# Revit family: LIANO II COMPACT TWIN SHWR 3S OHD
name_source: partatom
category: Plumbing Fixtures
units: mm (PartAtom-declared; Revit-internal decimal feet)

## family parameters
Cut with Voids When Loaded = No
Host = Face
OmniClass Number = 23.45.05.14.17
OmniClass Title = Showers
Part Type = Normal
Room Calculation Point = No
Round Connector Dimension = Use Diameter
Shared = No

## types (6) — shared parameters
Assembly Code = D2020300
CW Connection = Yes
HW Connection = Yes
Manufacturer = GWA Bathrooms & Kitchens
Material_Sprays = GWA-Plastic-General
URL = https://www.caroma.com.au
Vent Connection = No
Waste Connection = No
zero-valued in all types: Default Elevation

## per-type parameters (varying)
| type | Material_Base | Model |
| LIANO II COMPACT TWIN SHWR 3S OHD CH | GWA_Metal-Chrome | 96472C33A |
| LIANO II COMPACT TWIN SHWR 3S OHD BB | GWA_Metal-Brushed-Brass | 96472BB33A |
| LIANO II COMPACT TWIN SHWR 3S OHD BK | GWA-Metal-Black | 96472B33A |
| LIANO II COMPACT TWIN SHWR 3S OHD GM | GWA_Metal-Brushed-Gunmetal | 96472GM33A |
| LIANO II COMPACT TWIN SHWR 3S OHD BN | GWA_Metal-Brushed-Nickel | 96472BN33A |
| LIANO II COMPACT TWIN SHWR 3S OHD BBZ | GWA_Metal-Brushed-Bronze | 96472BBZ33A |

note: column(s) folded — value = type name in every type: Description

## geometry (parser evidence)
native form markers: Sweep x4
no freeform markers — native parametric forms only
